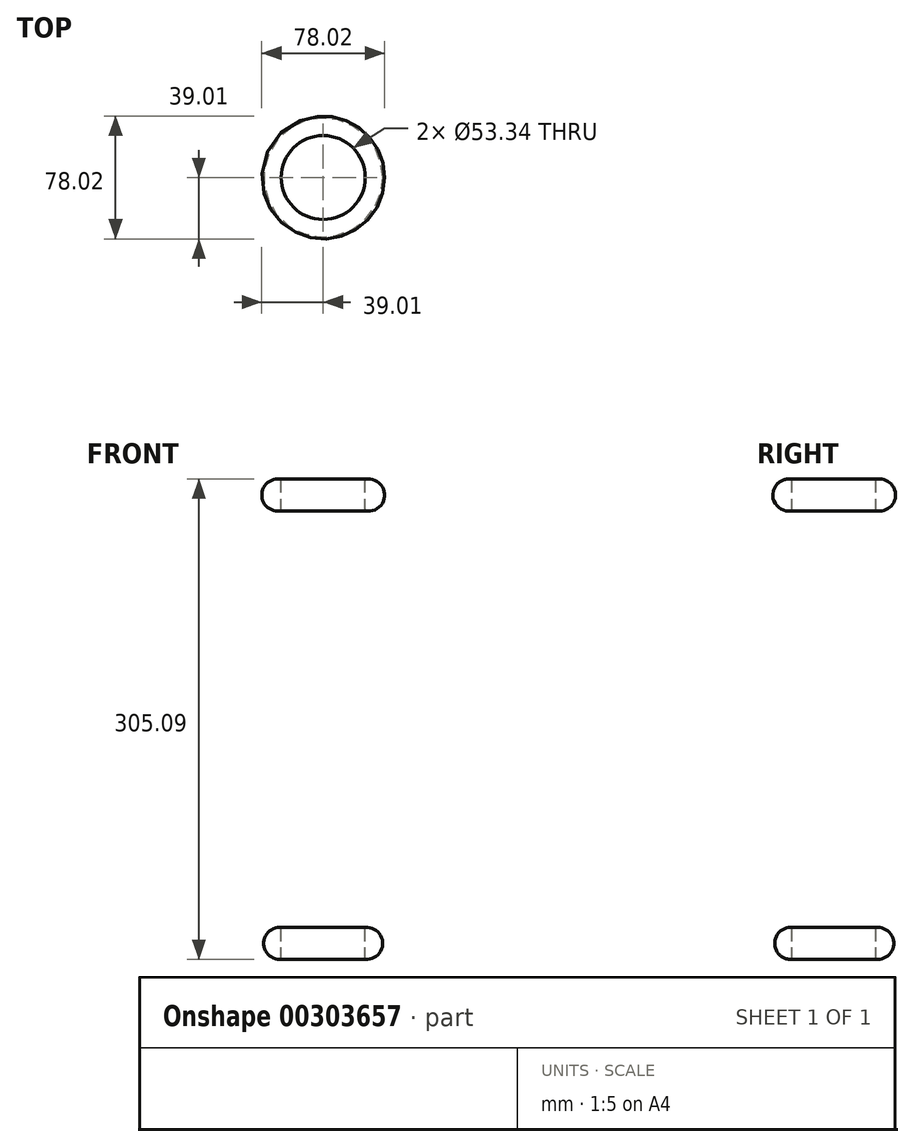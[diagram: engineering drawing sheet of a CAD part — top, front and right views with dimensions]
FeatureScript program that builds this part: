
annotation { "Feature Type Name" : "Feature", "Feature Type Description" : "" }
export const myFeature = defineFeature(function(context is Context, id is Id, definition is map)
    precondition{}
    {
        {
            var Q0;
            Q0=qCreatedBy(makeId("Front.planeOp"),FACE);
            var sketch = newSketch(context, id + "F0", { "sketchPlane" : qUnion([Q0])});
            skLineSegment(sketch, "E0", {"start": v(0, 74.85) * mm, "end": v(0, -74.85) * mm});
            skLineSegment(sketch, "E1", {"start": v(26.67, 74.85) * mm, "end": v(26.67, -229.95) * mm});
            skArc(sketch, "E2", {"start": v(26.67, -229.95) * mm, "mid": v(37.84, -219.84) * mm, "end": v(26.67, -209.73) * mm});
            skArc(sketch, "E3", {"start": v(26.67, 55) * mm, "mid": v(39, 64.93) * mm, "end": v(26.67, 74.85) * mm});
            skSolve(sketch);
        }
        {
            var Q0;
            Q0=sQuery(id+"F0.wireOp",EDGE,"E1");
            var Q1;
            Q1=sQuery(id+"F0.wireOp",EDGE,"E0");
            revolve(context, id + "F1", {"bodyType" : ToolBodyType.SURFACE, "surfaceEntities" : qUnion([Q0]), "axis" : qUnion([Q1]), "revolveType" : RevolveType.FULL});
        }
        {
            var Q0;
            {var subQ0=sQuery(id+"F0.wireOp",EDGE,"E3");Q0=makeQuery(id+"F0.imprint","IMPRINT",FACE,{"disambiguationData":[TD([[makeQuery(id+"F0.imprint","IMPRINT",EDGE,{"derivedFrom":subQ0}),1.0]])]});}
            var Q1;
            {var subQ0=sQuery(id+"F0.wireOp",EDGE,"E2");Q1=makeQuery(id+"F0.imprint","IMPRINT",FACE,{"disambiguationData":[TD([[makeQuery(id+"F0.imprint","IMPRINT",EDGE,{"derivedFrom":subQ0}),1.0]])]});}
            var Q2;
            Q2=sQuery(id+"F0.wireOp",EDGE,"E0");
            revolve(context, id + "F2", {"entities" : qUnion([Q0, Q1]), "axis" : qUnion([Q2]), "revolveType" : RevolveType.FULL});
        }
    });
